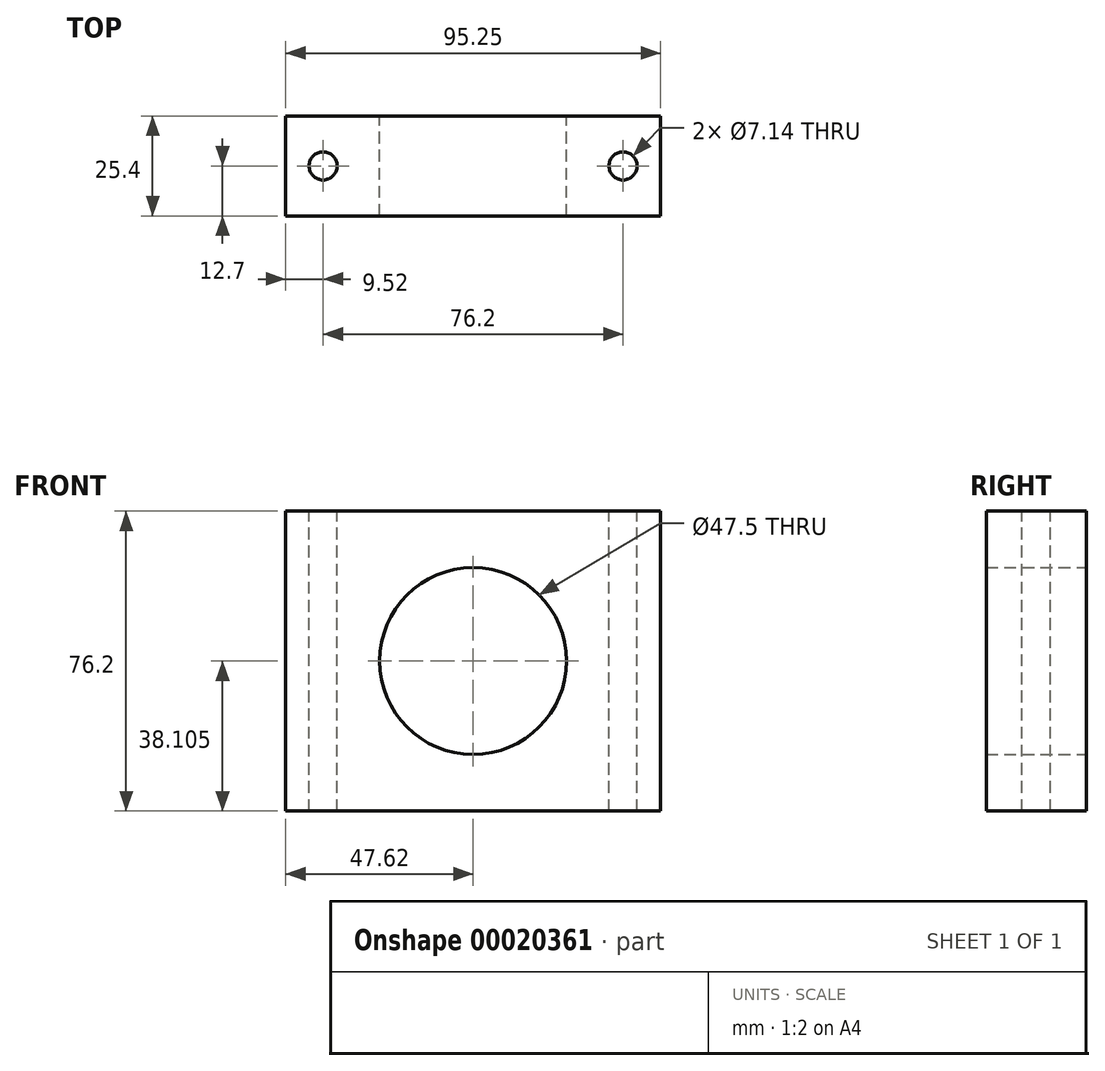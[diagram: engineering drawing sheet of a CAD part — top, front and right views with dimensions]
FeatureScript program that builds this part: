
annotation { "Feature Type Name" : "Feature", "Feature Type Description" : "" }
export const myFeature = defineFeature(function(context is Context, id is Id, definition is map)
    precondition{}
    {
        {
            var Q0;
            Q0=qCreatedBy(makeId("Front.planeOp"),FACE);
            var sketch = newSketch(context, id + "F0", { "sketchPlane" : qUnion([Q0])});
            skLineSegment(sketch, "E0.bottom", {"start": v(-47.62, 30.83) * mm, "end": v(47.63, 30.83) * mm});
            skLineSegment(sketch, "E0.top", {"start": v(-47.62, -45.37) * mm, "end": v(47.63, -45.37) * mm});
            skLineSegment(sketch, "E0.left", {"start": v(-47.62, 30.83) * mm, "end": v(-47.62, -45.37) * mm});
            skLineSegment(sketch, "E0.right", {"start": v(47.63, 30.83) * mm, "end": v(47.63, -45.37) * mm});
            skLineSegment(sketch, "E1", {"start": v(47.63, -7.27) * mm, "end": v(-47.62, -7.27) * mm, "construction": true});
            skCircle(sketch, "E2", {"center": v(0, -7.27) * mm, "radius": 23.75 * mm});
            skSolve(sketch);
        }
        {
            var Q0;
            Q0 = qSketchRegion(id + "F0", true);
            extrude(context, id + "F1", {"entities" : qUnion([Q0]), "depth" : 25.4 * mm});
        }
        {
            var Q0;
            Q0=makeQuery(id+"F1.opExtrude","SWEPT_FACE",FACE,{"disambiguationData":[OSD([sQuery(id+"F0.wireOp",EDGE,"E0.bottom")])]});
            var sketch = newSketch(context, id + "F2", { "sketchPlane" : qUnion([Q0])});
            skLineSegment(sketch, "E3.0", {"start": v(38.1, -25.4) * mm, "end": v(38.1, 0) * mm, "construction": true});
            skLineSegment(sketch, "E4", {"start": v(0, -25.4) * mm, "end": v(0, 0) * mm, "construction": true});
            skLineSegment(sketch, "E5.0", {"start": v(-47.62, -12.7) * mm, "end": v(47.63, -12.7) * mm, "construction": true});
            skCircle(sketch, "E6", {"center": v(38.1, -12.7) * mm, "radius": 3.57 * mm});
            skCircle(sketch, "E7.MirrorC", {"center": v(-38.1, -12.7) * mm, "radius": 3.57 * mm});
            skSolve(sketch);
        }
        {
            var Q0;
            Q0 = qSketchRegion(id + "F2", true);
            extrude(context, id + "F3", {"entities" : qUnion([Q0]), "operationType" : NewBodyOperationType.REMOVE, "endBound" : BoundingType.THROUGH_ALL, "oppositeDirection" : true, "depth" : 25.4 * mm});
        }
    });
